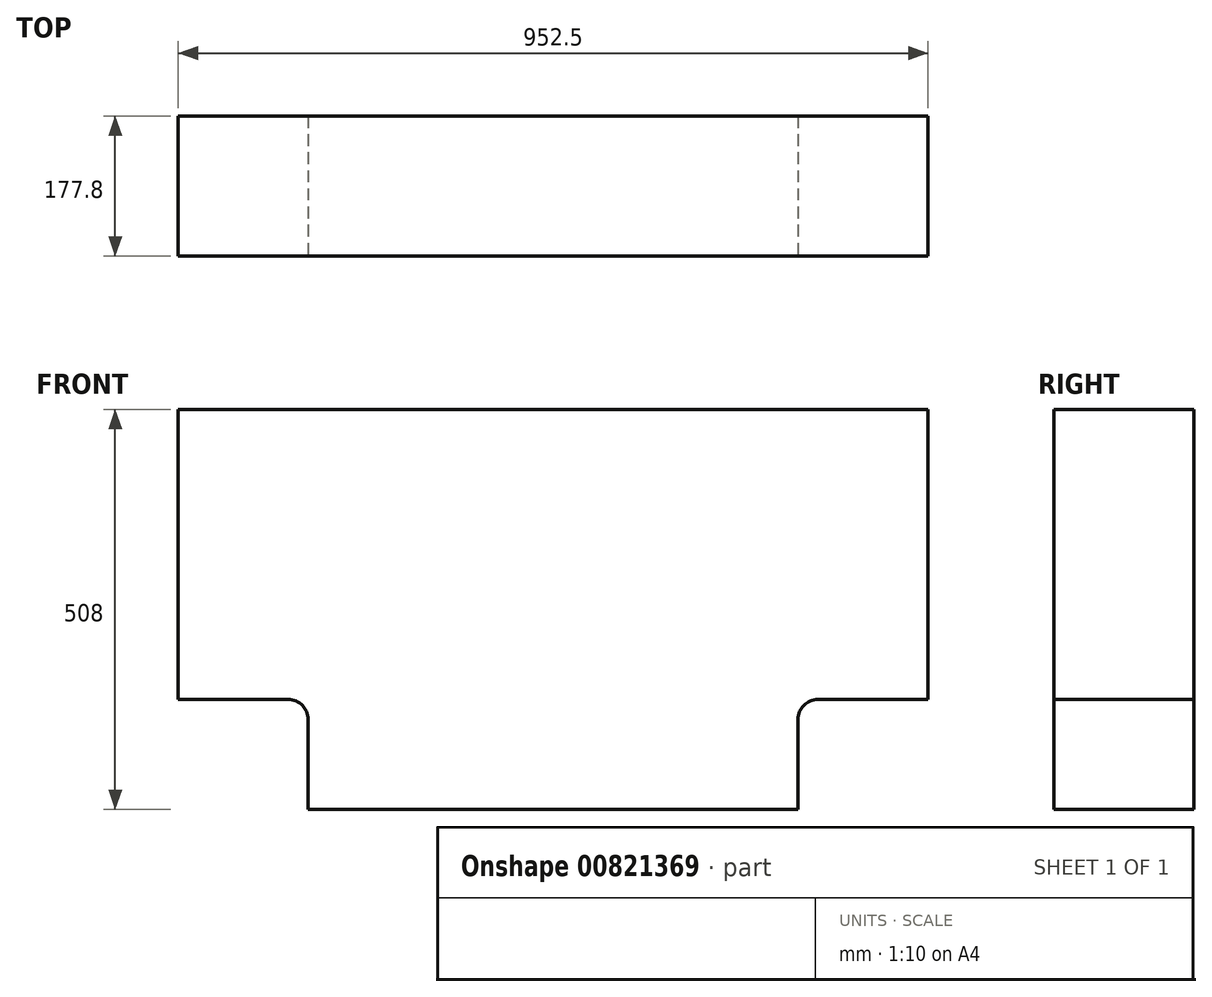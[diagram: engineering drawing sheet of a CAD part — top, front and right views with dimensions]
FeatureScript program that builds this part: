
annotation { "Feature Type Name" : "Feature", "Feature Type Description" : "" }
export const myFeature = defineFeature(function(context is Context, id is Id, definition is map)
    precondition{}
    {
        {
            var Q0;
            Q0=qCreatedBy(makeId("Front.planeOp"),FACE);
            var sketch = newSketch(context, id + "F0", { "sketchPlane" : qUnion([Q0])});
            skLineSegment(sketch, "E0.bottom", {"start": v(0, 0) * mm, "end": v(952.5, 0) * mm});
            skLineSegment(sketch, "E0.top", {"start": v(0, 508) * mm, "end": v(952.5, 508) * mm});
            skLineSegment(sketch, "E0.left", {"start": v(0, 0) * mm, "end": v(0, 508) * mm});
            skLineSegment(sketch, "E0.right", {"start": v(952.5, 0) * mm, "end": v(952.5, 508) * mm});
            skSolve(sketch);
        }
        {
            var Q0;
            Q0=makeQuery(id+"F0.imprint","IMPRINT",FACE,{"disambiguationData":[TD([[makeQuery(id+"F0.imprint","IMPRINT",EDGE,{"derivedFrom":sQuery(id+"F0.wireOp",EDGE,"E0.bottom")}),1.0]])]});
            extrude(context, id + "F1", {"entities" : qUnion([Q0]), "depth" : 177.8 * mm, "offsetDistance" : 25.4 * mm});
        }
        {
            var Q0;
            Q0=makeQuery(id+"F1.opExtrude","CAP_FACE",FACE,{"disambiguationData":[OSD([sQuery(id+"F0.wireOp",EDGE,"E0.bottom"),sQuery(id+"F0.wireOp",EDGE,"E0.top"),sQuery(id+"F0.wireOp",EDGE,"E0.left"),sQuery(id+"F0.wireOp",EDGE,"E0.right")])],"isStart":false});
            var sketch = newSketch(context, id + "F2", { "sketchPlane" : qUnion([Q0])});
            skLineSegment(sketch, "E1.bottom", {"start": v(0, 0) * mm, "end": v(165.1, 0) * mm});
            skLineSegment(sketch, "E1.top", {"start": v(0, 139.7) * mm, "end": v(165.1, 139.7) * mm});
            skLineSegment(sketch, "E1.left", {"start": v(0, 0) * mm, "end": v(0, 139.7) * mm});
            skLineSegment(sketch, "E1.right", {"start": v(165.1, 0) * mm, "end": v(165.1, 139.7) * mm});
            skLineSegment(sketch, "E2.bottom", {"start": v(952.5, 0) * mm, "end": v(787.4, 0) * mm});
            skLineSegment(sketch, "E2.top", {"start": v(952.5, 139.7) * mm, "end": v(787.4, 139.7) * mm});
            skLineSegment(sketch, "E2.left", {"start": v(952.5, 0) * mm, "end": v(952.5, 139.7) * mm});
            skLineSegment(sketch, "E2.right", {"start": v(787.4, 0) * mm, "end": v(787.4, 139.7) * mm});
            skSolve(sketch);
        }
        {
            var Q0;
            Q0 = qSketchRegion(id + "F2", true);
            extrude(context, id + "F3", {"entities" : qUnion([Q0]), "operationType" : NewBodyOperationType.REMOVE, "endBound" : BoundingType.THROUGH_ALL, "oppositeDirection" : true, "depth" : 25.4 * mm, "offsetDistance" : 25.4 * mm});
        }
        {
            var Q0;
            Q0=makeQuery(id+"F3.boolean.opBoolean","COPY",EDGE,{"derivedFrom":makeQuery(id+"F3.opExtrude","SWEPT_EDGE",EDGE,{"disambiguationData":[OSD([sQuery(id+"F2.wireOp",EDGE,"E1.top"),sQuery(id+"F2.wireOp",EDGE,"E1.right")])]})});
            var Q1;
            Q1=makeQuery(id+"F3.boolean.opBoolean","COPY",EDGE,{"derivedFrom":makeQuery(id+"F3.opExtrude","SWEPT_EDGE",EDGE,{"disambiguationData":[OSD([sQuery(id+"F2.wireOp",EDGE,"E2.top"),sQuery(id+"F2.wireOp",EDGE,"E2.right")])]})});
            fillet(context, id + "F4", {"entities" : qUnion([Q0, Q1]), "radius" : 25.4 * mm, "tangentPropagation" : true, "allowEdgeOverflow" : false});
        }
    });
